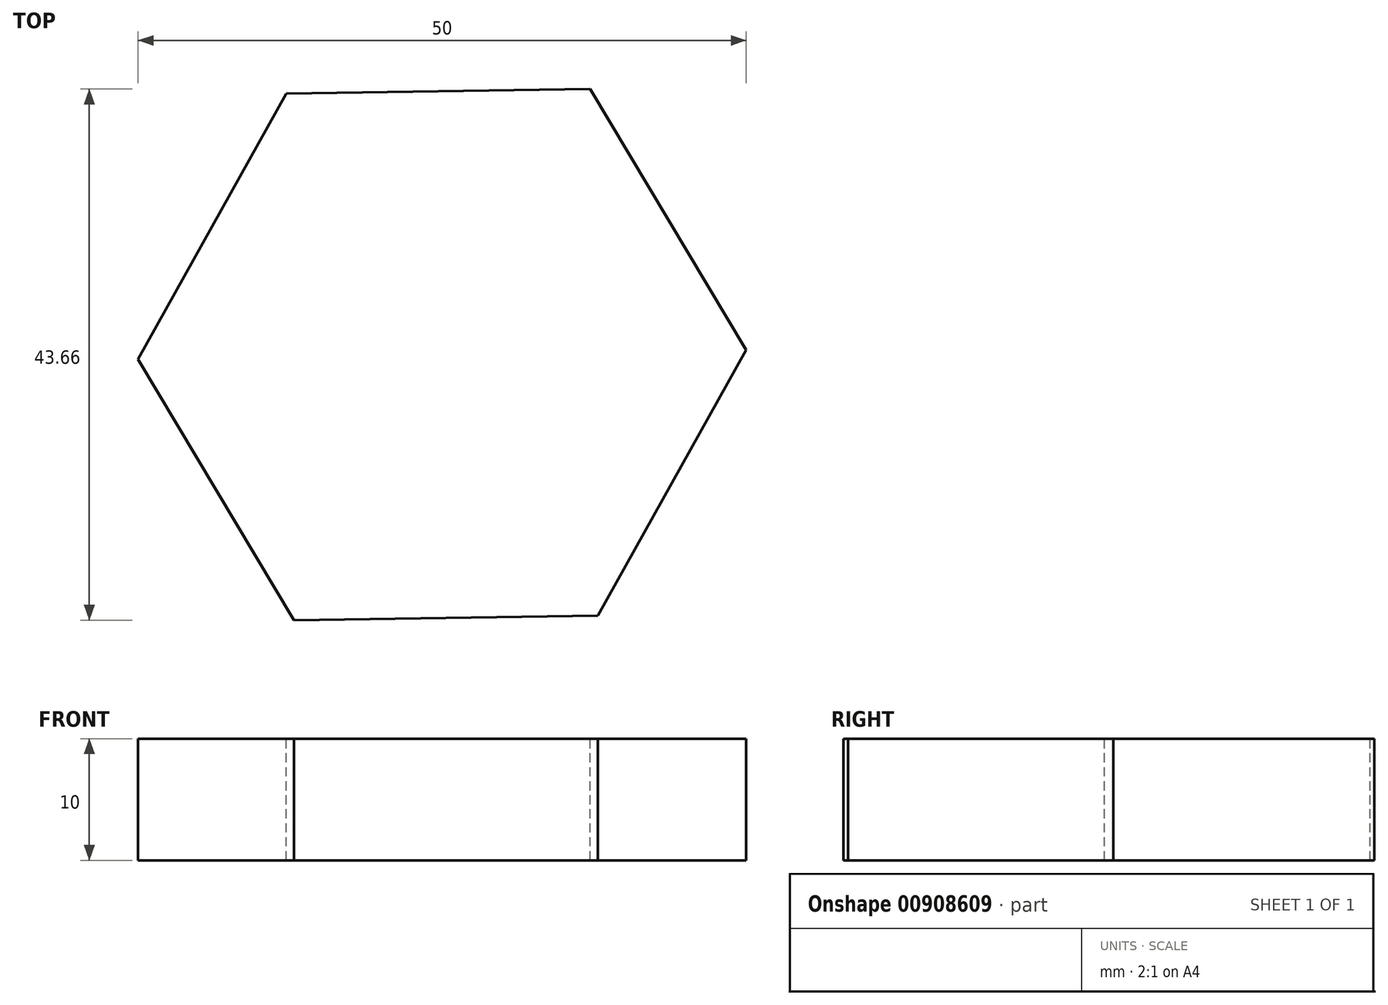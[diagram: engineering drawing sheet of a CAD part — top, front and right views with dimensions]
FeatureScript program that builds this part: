
annotation { "Feature Type Name" : "Feature", "Feature Type Description" : "" }
export const myFeature = defineFeature(function(context is Context, id is Id, definition is map)
    precondition{}
    {
        {
            var Q0;
            Q0=qCreatedBy(makeId("Top.planeOp"),FACE);
            var sketch = newSketch(context, id + "F0", { "sketchPlane" : qUnion([Q0])});
            skCircle(sketch, "E0.cCircle", {"center": v(0, 0) * mm, "radius": 21.65 * mm, "construction": true});
            skLineSegment(sketch, "E0.0", {"start": v(12.18, 21.83) * mm, "end": v(25, 0.37) * mm});
            skLineSegment(sketch, "E0.1", {"start": v(25, 0.37) * mm, "end": v(12.82, -21.46) * mm});
            skLineSegment(sketch, "E0.2", {"start": v(12.82, -21.46) * mm, "end": v(-12.18, -21.83) * mm});
            skLineSegment(sketch, "E0.3", {"start": v(-12.18, -21.83) * mm, "end": v(-25, -0.37) * mm});
            skLineSegment(sketch, "E0.4", {"start": v(-25, -0.37) * mm, "end": v(-12.82, 21.46) * mm});
            skLineSegment(sketch, "E0.5", {"start": v(-12.82, 21.46) * mm, "end": v(12.18, 21.83) * mm});
            skPoint(sketch, "E0.0.midPoint", {"position": v(18.59, 11.1) * mm});
            skSolve(sketch);
        }
        {
            var Q0;
            Q0=makeQuery(id+"F0.imprint","IMPRINT",FACE,{"disambiguationData":[TD([[makeQuery(id+"F0.imprint","IMPRINT",EDGE,{"derivedFrom":sQuery(id+"F0.wireOp",EDGE,"E0.0")}),-1.0]])]});
            var Q1;
            Q1=makeQuery(id+"F0.imprint","IMPRINT",FACE,{"disambiguationData":[TD([[makeQuery(id+"F0.imprint","IMPRINT",EDGE,{"derivedFrom":sQuery(id+"F0.wireOp",EDGE,"E0.0")}),-1.0]])]});
            extrude(context, id + "F1", {"entities" : qUnion([Q0, Q1]), "oppositeDirection" : true, "depth" : 10 * mm, "offsetDistance" : 25 * mm});
        }
    });
